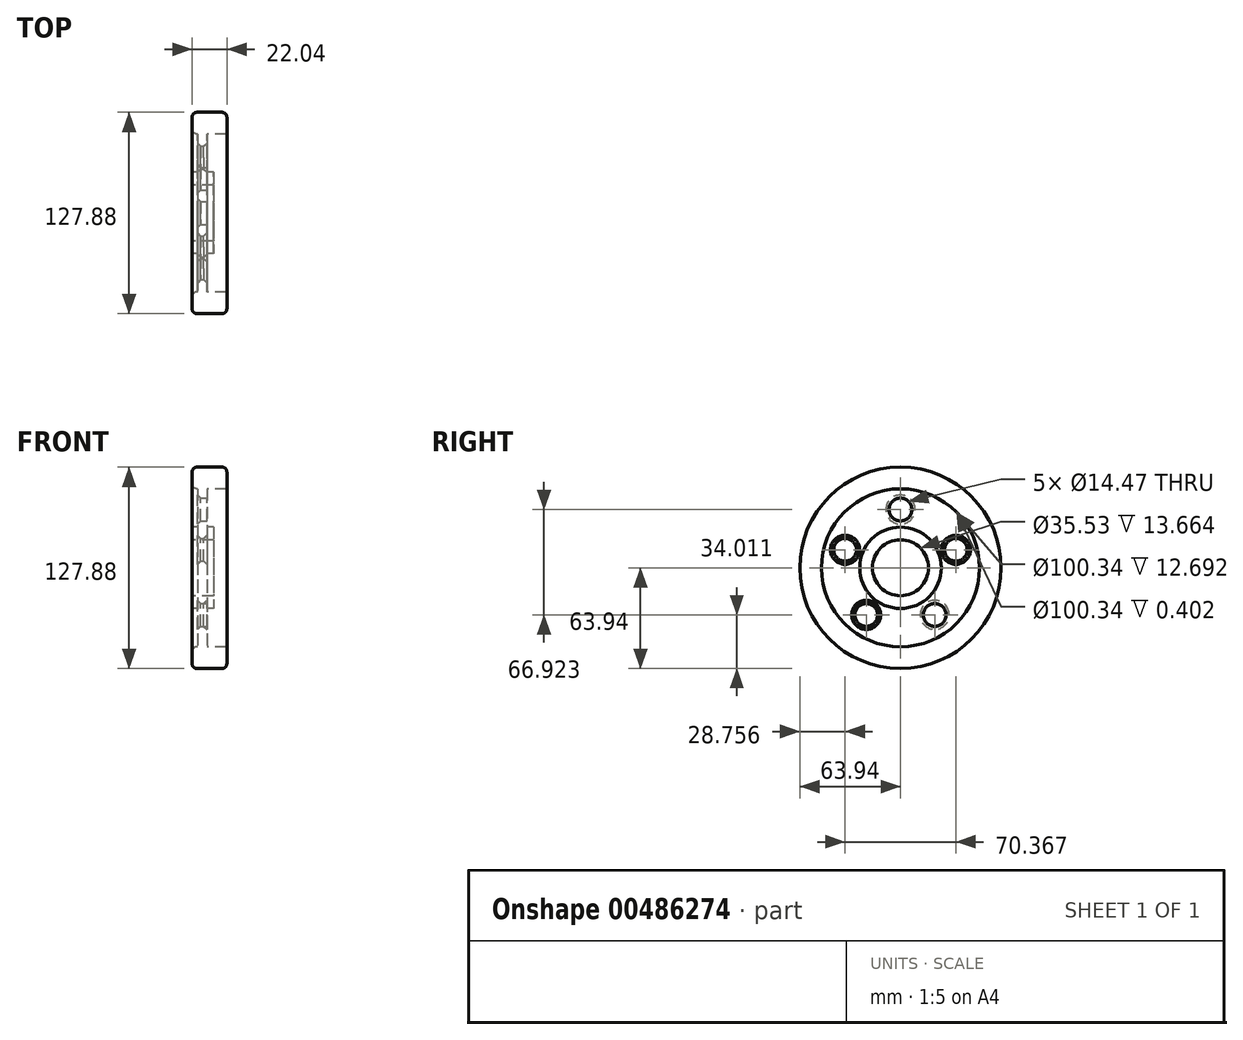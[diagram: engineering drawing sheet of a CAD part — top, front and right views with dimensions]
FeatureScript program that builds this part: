
annotation { "Feature Type Name" : "Feature", "Feature Type Description" : "" }
export const myFeature = defineFeature(function(context is Context, id is Id, definition is map)
    precondition{}
    {
        {
            var Q0;
            Q0=qCreatedBy(makeId("Front.planeOp"),FACE);
            var sketch = newSketch(context, id + "F0", { "sketchPlane" : qUnion([Q0])});
            skLineSegment(sketch, "E0", {"start": v(0, 0) * mm, "end": v(13.66, 0) * mm});
            skLineSegment(sketch, "E1", {"start": v(0, 17.77) * mm, "end": v(13.66, 17.77) * mm});
            skLineSegment(sketch, "E2", {"start": v(13.66, 17.77) * mm, "end": v(13.66, 25.87) * mm});
            skLineSegment(sketch, "E3", {"start": v(13.66, 25.87) * mm, "end": v(9.34, 25.87) * mm});
            skLineSegment(sketch, "E4", {"start": v(9.34, 25.87) * mm, "end": v(9.34, 50.17) * mm});
            skLineSegment(sketch, "E5", {"start": v(9.34, 50.17) * mm, "end": v(22.04, 50.17) * mm});
            skLineSegment(sketch, "E6", {"start": v(22.04, 50.17) * mm, "end": v(22.04, 63.94) * mm});
            skLineSegment(sketch, "E7", {"start": v(22.04, 63.94) * mm, "end": v(0, 63.94) * mm});
            skLineSegment(sketch, "E8", {"start": v(0, 63.94) * mm, "end": v(0, 50.17) * mm});
            skLineSegment(sketch, "E9", {"start": v(0, 50.17) * mm, "end": v(3.4, 50.17) * mm});
            skLineSegment(sketch, "E10", {"start": v(3.4, 50.17) * mm, "end": v(3.4, 25.87) * mm});
            skLineSegment(sketch, "E11", {"start": v(3.4, 25.87) * mm, "end": v(0, 25.87) * mm});
            skLineSegment(sketch, "E12", {"start": v(0, 25.87) * mm, "end": v(0, 17.77) * mm});
            skSolve(sketch);
        }
        {
            var Q0;
            Q0=makeQuery(id+"F0.imprint","IMPRINT",FACE,{"disambiguationData":[TD([[makeQuery(id+"F0.imprint","IMPRINT",EDGE,{"derivedFrom":sQuery(id+"F0.wireOp",EDGE,"E1")}),1.0]])]});
            var Q1;
            Q1=sQuery(id+"F0.wireOp",EDGE,"E0");
            revolve(context, id + "F1", {"entities" : qUnion([Q0]), "axis" : qUnion([Q1]), "revolveType" : RevolveType.FULL});
        }
        {
            var Q0;
            Q0=makeQuery(id+"F1.opRevolve","SWEPT_FACE",FACE,{"disambiguationData":[OSD([sQuery(id+"F0.wireOp",EDGE,"E4")])]});
            var sketch = newSketch(context, id + "F2", { "sketchPlane" : qUnion([Q0])});
            skCircle(sketch, "E13", {"center": v(0, 37) * mm, "radius": 7.23 * mm});
            skCircle(sketch, "E14.1.0", {"center": v(-35.18, 11.43) * mm, "radius": 7.23 * mm});
            skCircle(sketch, "E14.2.0", {"center": v(-21.74, -29.93) * mm, "radius": 7.23 * mm});
            skCircle(sketch, "E14.3.0", {"center": v(21.74, -29.93) * mm, "radius": 7.23 * mm});
            skCircle(sketch, "E14.4.0", {"center": v(35.18, 11.43) * mm, "radius": 7.23 * mm});
            skPoint(sketch, "E14.center", {"position": v(0, 0) * mm});
            skSolve(sketch);
        }
        {
            var Q0;
            Q0=makeQuery(id+"F2.imprint","IMPRINT",FACE,{"disambiguationData":[TD([[makeQuery(id+"F2.imprint","IMPRINT",EDGE,{"derivedFrom":sQuery(id+"F2.wireOp",EDGE,"E13")}),1.0]])]});
            var Q1;
            Q1=makeQuery(id+"F2.imprint","IMPRINT",FACE,{"disambiguationData":[TD([[makeQuery(id+"F2.imprint","IMPRINT",EDGE,{"derivedFrom":sQuery(id+"F2.wireOp",EDGE,"E14.2.0")}),1.0]])]});
            var Q2;
            Q2=makeQuery(id+"F2.imprint","IMPRINT",FACE,{"disambiguationData":[TD([[makeQuery(id+"F2.imprint","IMPRINT",EDGE,{"derivedFrom":sQuery(id+"F2.wireOp",EDGE,"E14.3.0")}),1.0]])]});
            var Q3;
            Q3=makeQuery(id+"F2.imprint","IMPRINT",FACE,{"disambiguationData":[TD([[makeQuery(id+"F2.imprint","IMPRINT",EDGE,{"derivedFrom":sQuery(id+"F2.wireOp",EDGE,"E14.4.0")}),1.0]])]});
            var Q4;
            Q4=makeQuery(id+"F2.imprint","IMPRINT",FACE,{"disambiguationData":[TD([[makeQuery(id+"F2.imprint","IMPRINT",EDGE,{"derivedFrom":sQuery(id+"F2.wireOp",EDGE,"E14.1.0")}),1.0]])]});
            extrude(context, id + "F3", {"entities" : qUnion([Q0, Q1, Q2, Q3, Q4]), "operationType" : NewBodyOperationType.REMOVE, "oppositeDirection" : true, "depth" : 25 * mm});
        }
        {
            var Q0;
            Q0=makeQuery(id+"F1.opRevolve","SWEPT_EDGE",EDGE,{"disambiguationData":[OSD([sQuery(id+"F0.wireOp",EDGE,"E6"),sQuery(id+"F0.wireOp",EDGE,"E7")])]});
            var Q1;
            Q1=makeQuery(id+"F1.opRevolve","SWEPT_FACE",FACE,{"disambiguationData":[OSD([sQuery(id+"F0.wireOp",EDGE,"E8")])]});
            fillet(context, id + "F4", {"entities" : qUnion([Q0, Q1]), "radius" : 3 * mm, "tangentPropagation" : true, "allowEdgeOverflow" : false});
        }
        {
            var Q0;
            Q0=makeQuery(id+"F3.boolean.opBoolean","INTERSECT",EDGE,{"derivedFrom":[makeQuery(id+"F1.opRevolve","SWEPT_FACE",FACE,{"disambiguationData":[OSD([sQuery(id+"F0.wireOp",EDGE,"E10")])]}),makeQuery(id+"F3.opExtrude","SWEPT_FACE",FACE,{"disambiguationData":[OSD([sQuery(id+"F2.wireOp",EDGE,"E13")])]})]});
            var Q1;
            Q1=makeQuery(id+"F3.boolean.opBoolean","COPY",FACE,{"derivedFrom":makeQuery(id+"F3.opExtrude","SWEPT_FACE",FACE,{"disambiguationData":[OSD([sQuery(id+"F2.wireOp",EDGE,"E14.4.0")])]})});
            var Q2;
            Q2=makeQuery(id+"F3.boolean.opBoolean","COPY",FACE,{"derivedFrom":makeQuery(id+"F3.opExtrude","SWEPT_FACE",FACE,{"disambiguationData":[OSD([sQuery(id+"F2.wireOp",EDGE,"E14.1.0")])]})});
            var Q3;
            Q3=makeQuery(id+"F3.boolean.opBoolean","COPY",FACE,{"derivedFrom":makeQuery(id+"F3.opExtrude","SWEPT_FACE",FACE,{"disambiguationData":[OSD([sQuery(id+"F2.wireOp",EDGE,"E14.2.0")])]})});
            var Q4;
            Q4=makeQuery(id+"F3.boolean.opBoolean","INTERSECT",EDGE,{"derivedFrom":[makeQuery(id+"F1.opRevolve","SWEPT_FACE",FACE,{"disambiguationData":[OSD([sQuery(id+"F0.wireOp",EDGE,"E10")])]}),makeQuery(id+"F3.opExtrude","SWEPT_FACE",FACE,{"disambiguationData":[OSD([sQuery(id+"F2.wireOp",EDGE,"E14.3.0")])]})]});
            chamfer(context, id + "F5", {"entities" : qUnion([Q0, Q1, Q2, Q3, Q4]), "width" : 2 * mm, "tangentPropagation" : true});
        }
    });
